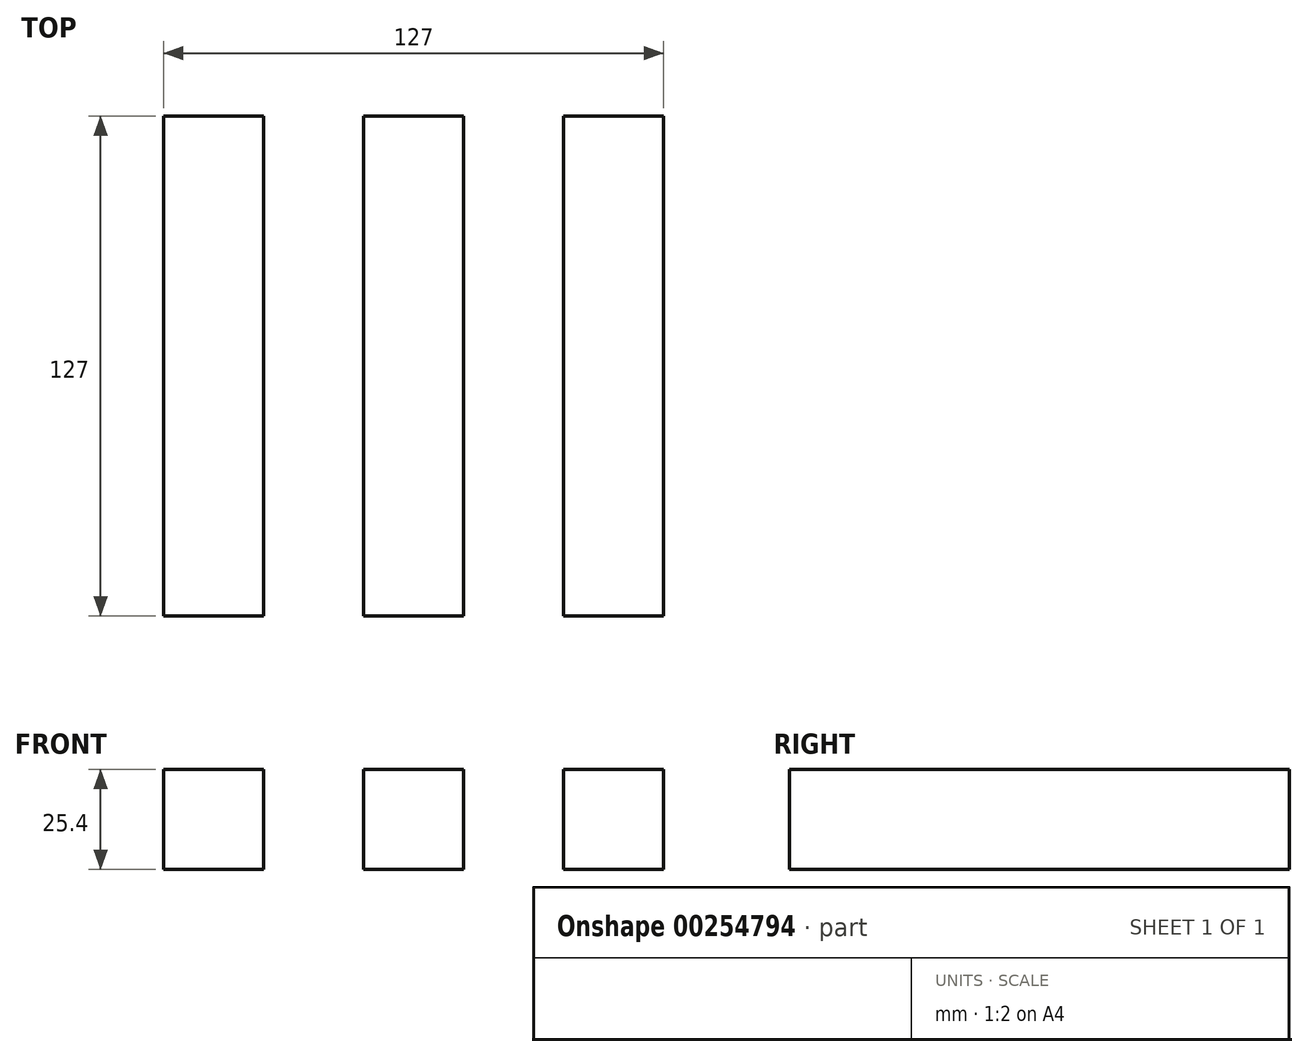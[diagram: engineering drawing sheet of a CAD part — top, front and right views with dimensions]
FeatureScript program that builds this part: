
annotation { "Feature Type Name" : "Feature", "Feature Type Description" : "" }
export const myFeature = defineFeature(function(context is Context, id is Id, definition is map)
    precondition{}
    {
        {
            var Q0;
            Q0=qCreatedBy(makeId("Front.planeOp"),FACE);
            var sketch = newSketch(context, id + "F0", { "sketchPlane" : qUnion([Q0])});
            skLineSegment(sketch, "E0.bottom", {"start": v(-12.7, 12.7) * mm, "end": v(12.7, 12.7) * mm});
            skLineSegment(sketch, "E0.top", {"start": v(-12.7, -12.7) * mm, "end": v(12.7, -12.7) * mm});
            skLineSegment(sketch, "E0.left", {"start": v(-12.7, 12.7) * mm, "end": v(-12.7, -12.7) * mm});
            skLineSegment(sketch, "E0.right", {"start": v(12.7, 12.7) * mm, "end": v(12.7, -12.7) * mm});
            skPoint(sketch, "E0.middle", {"position": v(0, 0) * mm});
            skLineSegment(sketch, "E1", {"start": v(0, 0) * mm, "end": v(-50.8, 0) * mm});
            skLineSegment(sketch, "E2", {"start": v(0, 0) * mm, "end": v(50.8, 0) * mm});
            skLineSegment(sketch, "E3.bottom", {"start": v(-63.5, 12.7) * mm, "end": v(-38.1, 12.7) * mm});
            skLineSegment(sketch, "E3.top", {"start": v(-63.5, -12.7) * mm, "end": v(-38.1, -12.7) * mm});
            skLineSegment(sketch, "E3.left", {"start": v(-63.5, 12.7) * mm, "end": v(-63.5, -12.7) * mm});
            skLineSegment(sketch, "E3.right", {"start": v(-38.1, 12.7) * mm, "end": v(-38.1, -12.7) * mm});
            skPoint(sketch, "E3.middle", {"position": v(-50.8, 0) * mm});
            skLineSegment(sketch, "E4.bottom", {"start": v(63.5, 12.7) * mm, "end": v(38.1, 12.7) * mm});
            skLineSegment(sketch, "E4.top", {"start": v(63.5, -12.7) * mm, "end": v(38.1, -12.7) * mm});
            skLineSegment(sketch, "E4.left", {"start": v(63.5, 12.7) * mm, "end": v(63.5, -12.7) * mm});
            skLineSegment(sketch, "E4.right", {"start": v(38.1, 12.7) * mm, "end": v(38.1, -12.7) * mm});
            skPoint(sketch, "E4.middle", {"position": v(50.8, 0) * mm});
            skSolve(sketch);
        }
        {
            var Q0;
            {var subQ1=sQuery(id+"F0.wireOp",EDGE,"E3.bottom");Q0=makeQuery(id+"F0.imprint","IMPRINT",FACE,{"disambiguationData":[TD([[makeQuery(id+"F0.imprint","IMPRINT",EDGE,{"derivedFrom":subQ1}),-1.0]])]});}
            var Q1;
            {var subQ1=sQuery(id+"F0.wireOp",EDGE,"E4.bottom");Q1=makeQuery(id+"F0.imprint","IMPRINT",FACE,{"disambiguationData":[TD([[makeQuery(id+"F0.imprint","IMPRINT",EDGE,{"derivedFrom":subQ1}),1.0]])]});}
            var Q2;
            {var subQ6=sQuery(id+"F0.wireOp",EDGE,"E0.bottom");Q2=makeQuery(id+"F0.imprint","IMPRINT",FACE,{"disambiguationData":[TD([[makeQuery(id+"F0.imprint","IMPRINT",EDGE,{"derivedFrom":subQ6}),-1.0]])]});}
            var Q3;
            {var subQ6=sQuery(id+"F0.wireOp",EDGE,"E0.top");Q3=makeQuery(id+"F0.imprint","IMPRINT",FACE,{"disambiguationData":[TD([[makeQuery(id+"F0.imprint","IMPRINT",EDGE,{"derivedFrom":subQ6}),1.0]])]});}
            extrude(context, id + "F1", {"entities" : qUnion([Q0, Q1, Q2, Q3]), "endBound" : BoundingType.SYMMETRIC, "depth" : 127 * mm});
        }
    });
